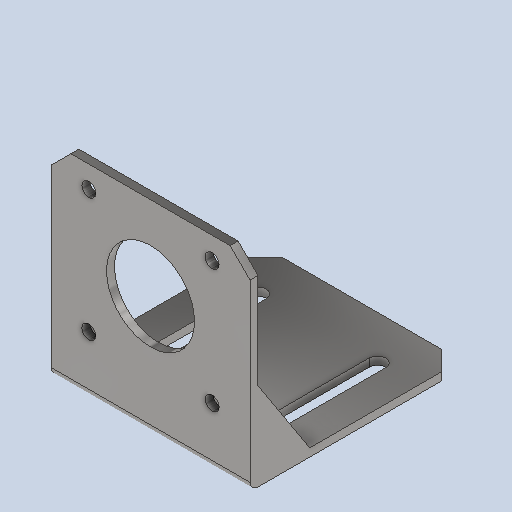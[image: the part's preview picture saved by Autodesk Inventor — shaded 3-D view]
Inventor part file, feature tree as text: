
AUTODESK INVENTOR PART (.ipt)
format: ipt  version: 2025.1 (Build 291241000, 241)  size: 166,912 bytes
history: native  units: mm
features: other x4, sketch x3
ambient origin geometry x8: Origin, YZ Plane, XZ Plane, XY Plane, X Axis, Y Axis, Z Axis, Center Point
bodies: Body1 (feature_tree)
feature tree (7):
  other  "NEMA17MountingLBracket.ipt"
  other  "Sólido1::NEMA17MountingLBracket.ipt"
  other  "OperaçãoIdentificador1"
  sketch  "Boceto1"  dims[d0=10.0mm]
  sketch  "Boceto2"
  sketch  "Boceto3"
  other  "Sólido1"
